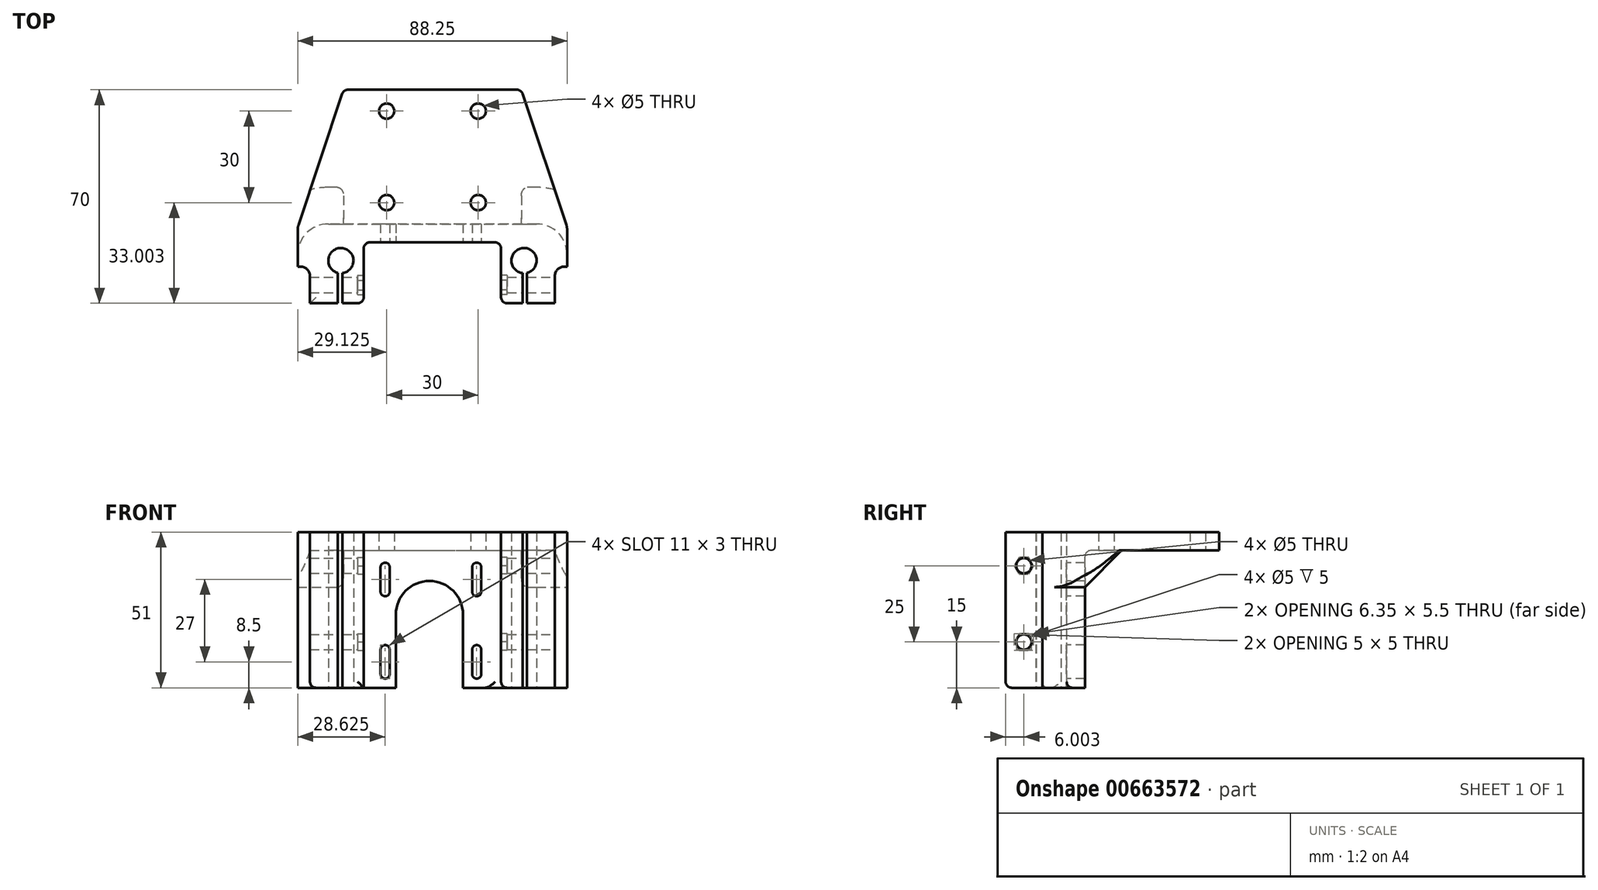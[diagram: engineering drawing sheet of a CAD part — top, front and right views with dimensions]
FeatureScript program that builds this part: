
annotation { "Feature Type Name" : "Feature", "Feature Type Description" : "" }
export const myFeature = defineFeature(function(context is Context, id is Id, definition is map)
    precondition{}
    {
        {
            var Q0;
            Q0=qCreatedBy(makeId("Top.planeOp"),FACE);
            var sketch = newSketch(context, id + "F0", { "sketchPlane" : qUnion([Q0])});
            skLineSegment(sketch, "E0.bottom", {"start": v(-36.85, 32.58) * mm, "end": v(21.4, 32.58) * mm});
            skLineSegment(sketch, "E0.top", {"start": v(-51.85, -37.42) * mm, "end": v(36.4, -37.42) * mm});
            skLineSegment(sketch, "E0.left", {"start": v(-51.85, -12.42) * mm, "end": v(-51.85, -37.42) * mm});
            skLineSegment(sketch, "E0.right", {"start": v(36.4, -12.42) * mm, "end": v(36.4, -37.42) * mm});
            skLineSegment(sketch, "E1", {"start": v(-30.23, -37.42) * mm, "end": v(-30.23, -17.42) * mm});
            skLineSegment(sketch, "E2", {"start": v(-30.23, -17.42) * mm, "end": v(14.77, -17.42) * mm});
            skLineSegment(sketch, "E3", {"start": v(14.77, -17.42) * mm, "end": v(14.77, -37.42) * mm});
            skCircle(sketch, "E4", {"center": v(22.27, -23.42) * mm, "radius": 4.12 * mm});
            skCircle(sketch, "E5", {"center": v(-37.73, -23.42) * mm, "radius": 4.12 * mm});
            skCircle(sketch, "E6", {"center": v(-22.73, 25.58) * mm, "radius": 2.5 * mm});
            skCircle(sketch, "E7", {"center": v(7.27, 25.58) * mm, "radius": 2.5 * mm});
            skCircle(sketch, "E8", {"center": v(-22.73, -4.42) * mm, "radius": 2.5 * mm});
            skCircle(sketch, "E9", {"center": v(7.27, -4.42) * mm, "radius": 2.5 * mm});
            skLineSegment(sketch, "E10", {"start": v(-51.85, -12.42) * mm, "end": v(-36.85, 32.58) * mm});
            skLineSegment(sketch, "E11", {"start": v(36.4, -12.42) * mm, "end": v(21.4, 32.58) * mm});
            skSolve(sketch);
        }
        {
            var Q0;
            Q0=makeQuery(id+"F0.imprint","IMPRINT",FACE,{"disambiguationData":[TD([[makeQuery(id+"F0.imprint","IMPRINT",EDGE,{"derivedFrom":sQuery(id+"F0.wireOp",EDGE,"E0.bottom")}),-1.0]])]});
            extrude(context, id + "F1", {"entities" : qUnion([Q0]), "depth" : 55 * mm, "offsetDistance" : 25 * mm});
        }
        {
            var Q0;
            Q0=makeQuery(id+"F1.opExtrude","CAP_FACE",FACE,{"disambiguationData":[OSD([sQuery(id+"F0.wireOp",EDGE,"E0.bottom"),sQuery(id+"F0.wireOp",EDGE,"E0.top"),sQuery(id+"F0.wireOp",EDGE,"E0.left"),sQuery(id+"F0.wireOp",EDGE,"E0.right"),sQuery(id+"F0.wireOp",EDGE,"E1"),sQuery(id+"F0.wireOp",EDGE,"E2"),sQuery(id+"F0.wireOp",EDGE,"E3"),sQuery(id+"F0.wireOp",EDGE,"E4"),sQuery(id+"F0.wireOp",EDGE,"E5"),sQuery(id+"F0.wireOp",EDGE,"E6"),sQuery(id+"F0.wireOp",EDGE,"E7"),sQuery(id+"F0.wireOp",EDGE,"E8"),sQuery(id+"F0.wireOp",EDGE,"E9"),sQuery(id+"F0.wireOp",EDGE,"E10"),sQuery(id+"F0.wireOp",EDGE,"E11")])],"isStart":true});
            var sketch = newSketch(context, id + "F2", { "sketchPlane" : qUnion([Q0])});
            skLineSegment(sketch, "E12", {"start": v(30.89, -4.12) * mm, "end": v(16.4, 11.42) * mm});
            skLineSegment(sketch, "E13", {"start": v(16.4, 11.42) * mm, "end": v(-31.85, 11.42) * mm});
            skLineSegment(sketch, "E14", {"start": v(-31.85, 11.42) * mm, "end": v(-46.34, -4.12) * mm});
            skLineSegment(sketch, "E15", {"start": v(-46.34, -4.12) * mm, "end": v(-36.85, -32.58) * mm});
            skLineSegment(sketch, "E16", {"start": v(-36.85, -32.58) * mm, "end": v(21.4, -32.58) * mm});
            skLineSegment(sketch, "E17", {"start": v(21.4, -32.58) * mm, "end": v(30.89, -4.12) * mm});
            skSolve(sketch);
        }
        {
            var Q0;
            Q0=makeQuery(id+"F2.imprint","IMPRINT",FACE,{"disambiguationData":[TD([[makeQuery(id+"F2.imprint","IMPRINT",EDGE,{"derivedFrom":sQuery(id+"F2.wireOp",EDGE,"E12")}),1.0]])]});
            extrude(context, id + "F3", {"entities" : qUnion([Q0]), "operationType" : NewBodyOperationType.REMOVE, "oppositeDirection" : true, "depth" : 45 * mm, "offsetDistance" : 25 * mm});
        }
        {
            var Q0;
            Q0=makeQuery(id+"F1.opExtrude","SWEPT_FACE",FACE,{"disambiguationData":[OSD([sQuery(id+"F0.wireOp",EDGE,"E2")])]});
            var sketch = newSketch(context, id + "F4", { "sketchPlane" : qUnion([Q0])});
            skArc(sketch, "E18", {"start": v(2.27, 24) * mm, "mid": v(-8.73, 35) * mm, "end": v(-19.73, 24) * mm});
            skLineSegment(sketch, "E19", {"start": v(-19.73, 24) * mm, "end": v(-19.73, 0) * mm});
            skLineSegment(sketch, "E20", {"start": v(-19.73, 0) * mm, "end": v(2.27, 0) * mm});
            skLineSegment(sketch, "E21", {"start": v(2.27, 24) * mm, "end": v(2.27, 0) * mm});
            skSolve(sketch);
        }
        {
            var Q0;
            Q0=makeQuery(id+"F4.imprint","IMPRINT",FACE,{"disambiguationData":[TD([[makeQuery(id+"F4.imprint","IMPRINT",EDGE,{"derivedFrom":sQuery(id+"F4.wireOp",EDGE,"E18")}),1.0]])]});
            extrude(context, id + "F5", {"entities" : qUnion([Q0]), "operationType" : NewBodyOperationType.REMOVE, "oppositeDirection" : true, "depth" : 25 * mm, "offsetDistance" : 25 * mm});
        }
        {
            var Q0;
            {var subQ0=sQuery(id+"F0.wireOp",EDGE,"E1");var subQ1=sQuery(id+"F0.wireOp",EDGE,"E0.left");var subQ2=sQuery(id+"F0.wireOp",EDGE,"E10");var subQ3=sQuery(id+"F0.wireOp",EDGE,"E2");var subQ4=sQuery(id+"F0.wireOp",EDGE,"E0.top");var subQ5=sQuery(id+"F0.wireOp",EDGE,"E5");Q0=makeQuery(id+"F5.boolean.opBoolean","SPLIT",FACE,{"disambiguationData":[TD([makeQuery(id+"F1.opExtrude","SWEPT_FACE",FACE,{"disambiguationData":[OSD([subQ1])]})])],"derivedFrom":makeQuery(id+"F1.opExtrude","CAP_FACE",FACE,{"disambiguationData":[OSD([sQuery(id+"F0.wireOp",EDGE,"E0.bottom"),subQ4,subQ1,sQuery(id+"F0.wireOp",EDGE,"E0.right"),subQ0,subQ3,sQuery(id+"F0.wireOp",EDGE,"E3"),sQuery(id+"F0.wireOp",EDGE,"E4"),subQ5,sQuery(id+"F0.wireOp",EDGE,"E6"),sQuery(id+"F0.wireOp",EDGE,"E7"),sQuery(id+"F0.wireOp",EDGE,"E8"),sQuery(id+"F0.wireOp",EDGE,"E9"),subQ2,sQuery(id+"F0.wireOp",EDGE,"E11")])],"isStart":true})});}
            var sketch = newSketch(context, id + "F6", { "sketchPlane" : qUnion([Q0])});
            skLineSegment(sketch, "E22.bottom", {"start": v(-38.73, 37.42) * mm, "end": v(-37.23, 37.42) * mm});
            skLineSegment(sketch, "E22.top", {"start": v(-38.73, 26.54) * mm, "end": v(-37.23, 26.54) * mm});
            skLineSegment(sketch, "E22.left", {"start": v(-38.73, 37.42) * mm, "end": v(-38.73, 26.54) * mm});
            skLineSegment(sketch, "E22.right", {"start": v(-37.23, 37.42) * mm, "end": v(-37.23, 26.54) * mm});
            skLineSegment(sketch, "E23.bottom", {"start": v(21.77, 37.42) * mm, "end": v(23.27, 37.42) * mm});
            skLineSegment(sketch, "E23.top", {"start": v(21.77, 26.54) * mm, "end": v(23.27, 26.54) * mm});
            skLineSegment(sketch, "E23.left", {"start": v(21.77, 37.42) * mm, "end": v(21.77, 26.54) * mm});
            skLineSegment(sketch, "E23.right", {"start": v(23.27, 37.42) * mm, "end": v(23.27, 26.54) * mm});
            skSolve(sketch);
        }
        {
            var Q0;
            Q0=makeQuery(id+"F6.imprint","IMPRINT",FACE,{"disambiguationData":[TD([[makeQuery(id+"F6.imprint","IMPRINT",EDGE,{"derivedFrom":sQuery(id+"F6.wireOp",EDGE,"E23.bottom")}),-1.0]])]});
            var Q1;
            {var subQ0=sQuery(id+"F6.wireOp",EDGE,"E22.bottom");Q1=makeQuery(id+"F6.imprint","IMPRINT",FACE,{"disambiguationData":[TD([[makeQuery(id+"F6.imprint","IMPRINT",EDGE,{"derivedFrom":subQ0}),-1.0]])]});}
            extrude(context, id + "F7", {"entities" : qUnion([Q0, Q1]), "operationType" : NewBodyOperationType.REMOVE, "oppositeDirection" : true, "depth" : 55 * mm, "offsetDistance" : 25 * mm});
        }
        {
            var Q0;
            Q0=makeQuery(id+"F1.opExtrude","SWEPT_FACE",FACE,{"disambiguationData":[OSD([sQuery(id+"F0.wireOp",EDGE,"E0.right")])]});
            var sketch = newSketch(context, id + "F8", { "sketchPlane" : qUnion([Q0])});
            skCircle(sketch, "E24", {"center": v(-31.42, 15) * mm, "radius": 2.5 * mm});
            skCircle(sketch, "E25", {"center": v(-31.42, 40) * mm, "radius": 2.5 * mm});
            skSolve(sketch);
        }
        {
            var Q0;
            Q0=makeQuery(id+"F8.imprint","IMPRINT",FACE,{"disambiguationData":[TD([[makeQuery(id+"F8.imprint","IMPRINT",EDGE,{"derivedFrom":sQuery(id+"F8.wireOp",EDGE,"E24")}),1.0]])]});
            var Q1;
            Q1=makeQuery(id+"F8.imprint","IMPRINT",FACE,{"disambiguationData":[TD([[makeQuery(id+"F8.imprint","IMPRINT",EDGE,{"derivedFrom":sQuery(id+"F8.wireOp",EDGE,"E25")}),1.0]])]});
            extrude(context, id + "F9", {"entities" : qUnion([Q0, Q1]), "operationType" : NewBodyOperationType.REMOVE, "oppositeDirection" : true, "depth" : 100 * mm, "offsetDistance" : 25 * mm});
        }
        {
            var Q0;
            Q0=makeQuery(id+"F1.opExtrude","SWEPT_FACE",FACE,{"disambiguationData":[OSD([sQuery(id+"F0.wireOp",EDGE,"E0.bottom")])]});
            var sketch = newSketch(context, id + "F10", { "sketchPlane" : qUnion([Q0])});
            skLineSegment(sketch, "E26", {"start": v(51.85, 51) * mm, "end": v(-36.4, 51) * mm});
            skLineSegment(sketch, "E27", {"start": v(51.85, 51) * mm, "end": v(51.85, 51) * mm});
            skLineSegment(sketch, "E28", {"start": v(-36.4, 51) * mm, "end": v(-36.4, 51) * mm});
            skLineSegment(sketch, "E29", {"start": v(-36.4, 51) * mm, "end": v(-36.4, 55) * mm});
            skLineSegment(sketch, "E30", {"start": v(-36.4, 55) * mm, "end": v(51.85, 55) * mm});
            skLineSegment(sketch, "E31", {"start": v(51.85, 55) * mm, "end": v(51.85, 51) * mm});
            skSolve(sketch);
        }
        {
            var Q0;
            {var subQ0=sQuery(id+"F10.wireOp",EDGE,"E31");Q0=makeQuery(id+"F10.imprint","IMPRINT",FACE,{"disambiguationData":[TD([[makeQuery(id+"F10.imprint","IMPRINT",EDGE,{"derivedFrom":subQ0}),-1.0]])]});}
            var Q1;
            {var subQ0=sQuery(id+"F10.wireOp",EDGE,"E26");var subQ1=sQuery(id+"F0.wireOp",EDGE,"E0.bottom");var subQ2=makeQuery(id+"F1.opExtrude","SWEPT_EDGE",EDGE,{"disambiguationData":[OSD([subQ1,sQuery(id+"F0.wireOp",EDGE,"E10")])]});var subQ3=makeQuery(id+"F10.imprint","INTERSECT",VERTEX,{"derivedFrom":[subQ2,subQ0]});Q1=makeQuery(id+"F10.imprint","IMPRINT",FACE,{"disambiguationData":[TD([[makeQuery(id+"F10.imprint","IMPRINT",EDGE,{"disambiguationData":[TD([[subQ3,-1.0]])],"derivedFrom":subQ0}),-1.0]])]});}
            var Q2;
            {var subQ0=sQuery(id+"F10.wireOp",EDGE,"E29");Q2=makeQuery(id+"F10.imprint","IMPRINT",FACE,{"disambiguationData":[TD([[makeQuery(id+"F10.imprint","IMPRINT",EDGE,{"derivedFrom":subQ0}),-1.0]])]});}
            extrude(context, id + "F11", {"entities" : qUnion([Q0, Q1, Q2]), "operationType" : NewBodyOperationType.REMOVE, "oppositeDirection" : true, "depth" : 80 * mm, "offsetDistance" : 25 * mm});
        }
        {
            var Q0;
            Q0=makeQuery(id+"F1.opExtrude","SWEPT_FACE",FACE,{"disambiguationData":[OSD([sQuery(id+"F0.wireOp",EDGE,"E2")])]});
            var sketch = newSketch(context, id + "F12", { "sketchPlane" : qUnion([Q0])});
            skArc(sketch, "E32", {"start": v(-21.73, 39.5) * mm, "mid": v(-23.23, 41) * mm, "end": v(-24.73, 39.5) * mm});
            skArc(sketch, "E33", {"start": v(8.27, 39.5) * mm, "mid": v(6.77, 41) * mm, "end": v(5.27, 39.5) * mm});
            skArc(sketch, "E34", {"start": v(5.27, 4.5) * mm, "mid": v(6.77, 3) * mm, "end": v(8.27, 4.5) * mm});
            skArc(sketch, "E35", {"start": v(-24.73, 4.5) * mm, "mid": v(-23.23, 3) * mm, "end": v(-21.73, 4.5) * mm});
            skLineSegment(sketch, "E36", {"start": v(-21.73, 4.5) * mm, "end": v(-21.73, 12.5) * mm});
            skLineSegment(sketch, "E37", {"start": v(8.27, 39.5) * mm, "end": v(8.27, 31.5) * mm});
            skLineSegment(sketch, "E38", {"start": v(5.27, 4.5) * mm, "end": v(5.27, 12.5) * mm});
            skLineSegment(sketch, "E39", {"start": v(-24.73, 39.5) * mm, "end": v(-24.73, 31.5) * mm});
            skArc(sketch, "E40", {"start": v(8.27, 12.5) * mm, "mid": v(6.77, 14) * mm, "end": v(5.27, 12.5) * mm});
            skArc(sketch, "E41", {"start": v(5.27, 31.5) * mm, "mid": v(6.77, 30) * mm, "end": v(8.27, 31.5) * mm});
            skArc(sketch, "E42", {"start": v(-24.73, 31.5) * mm, "mid": v(-23.23, 30) * mm, "end": v(-21.73, 31.5) * mm});
            skArc(sketch, "E43", {"start": v(-21.73, 12.5) * mm, "mid": v(-23.23, 14) * mm, "end": v(-24.73, 12.5) * mm});
            skLineSegment(sketch, "E44.trimOffspring", {"start": v(8.27, 12.5) * mm, "end": v(8.27, 4.5) * mm});
            skLineSegment(sketch, "E45.trimOffspring", {"start": v(5.27, 31.5) * mm, "end": v(5.27, 39.5) * mm});
            skLineSegment(sketch, "E46.trimOffspring", {"start": v(-21.73, 31.5) * mm, "end": v(-21.73, 39.5) * mm});
            skLineSegment(sketch, "E47.trimOffspring", {"start": v(-24.73, 12.5) * mm, "end": v(-24.73, 4.5) * mm});
            skSolve(sketch);
        }
        {
            var Q0;
            Q0=makeQuery(id+"F12.imprint","IMPRINT",FACE,{"disambiguationData":[TD([[makeQuery(id+"F12.imprint","IMPRINT",EDGE,{"derivedFrom":sQuery(id+"F12.wireOp",EDGE,"E32")}),1.0]])]});
            var Q1;
            Q1=makeQuery(id+"F12.imprint","IMPRINT",FACE,{"disambiguationData":[TD([[makeQuery(id+"F12.imprint","IMPRINT",EDGE,{"derivedFrom":sQuery(id+"F12.wireOp",EDGE,"E35")}),1.0]])]});
            var Q2;
            Q2=makeQuery(id+"F12.imprint","IMPRINT",FACE,{"disambiguationData":[TD([[makeQuery(id+"F12.imprint","IMPRINT",EDGE,{"derivedFrom":sQuery(id+"F12.wireOp",EDGE,"E34")}),1.0]])]});
            var Q3;
            Q3=makeQuery(id+"F12.imprint","IMPRINT",FACE,{"disambiguationData":[TD([[makeQuery(id+"F12.imprint","IMPRINT",EDGE,{"derivedFrom":sQuery(id+"F12.wireOp",EDGE,"E33")}),1.0]])]});
            extrude(context, id + "F13", {"entities" : qUnion([Q0, Q1, Q2, Q3]), "operationType" : NewBodyOperationType.REMOVE, "oppositeDirection" : true, "depth" : 25 * mm, "offsetDistance" : 25 * mm});
        }
        {
            var Q0;
            {var subQ0=sQuery(id+"F0.wireOp",EDGE,"E1");var subQ1=sQuery(id+"F0.wireOp",EDGE,"E0.left");var subQ2=sQuery(id+"F0.wireOp",EDGE,"E10");var subQ3=sQuery(id+"F0.wireOp",EDGE,"E2");var subQ4=sQuery(id+"F0.wireOp",EDGE,"E0.top");var subQ5=sQuery(id+"F0.wireOp",EDGE,"E5");Q0=makeQuery(id+"F5.boolean.opBoolean","SPLIT",FACE,{"disambiguationData":[TD([makeQuery(id+"F1.opExtrude","SWEPT_FACE",FACE,{"disambiguationData":[OSD([subQ1])]})])],"derivedFrom":makeQuery(id+"F1.opExtrude","CAP_FACE",FACE,{"disambiguationData":[OSD([sQuery(id+"F0.wireOp",EDGE,"E0.bottom"),subQ4,subQ1,sQuery(id+"F0.wireOp",EDGE,"E0.right"),subQ0,subQ3,sQuery(id+"F0.wireOp",EDGE,"E3"),sQuery(id+"F0.wireOp",EDGE,"E4"),subQ5,sQuery(id+"F0.wireOp",EDGE,"E6"),sQuery(id+"F0.wireOp",EDGE,"E7"),sQuery(id+"F0.wireOp",EDGE,"E8"),sQuery(id+"F0.wireOp",EDGE,"E9"),subQ2,sQuery(id+"F0.wireOp",EDGE,"E11")])],"isStart":true})});}
            var sketch = newSketch(context, id + "F14", { "sketchPlane" : qUnion([Q0])});
            skLineSegment(sketch, "E48", {"start": v(-46.34, -4.12) * mm, "end": v(-31.85, 11.42) * mm});
            skLineSegment(sketch, "E49", {"start": v(-31.85, 11.42) * mm, "end": v(-51.52, 11.42) * mm});
            skLineSegment(sketch, "E50", {"start": v(-51.52, 11.42) * mm, "end": v(-46.34, -4.12) * mm});
            skLineSegment(sketch, "E51", {"start": v(16.4, 11.42) * mm, "end": v(30.89, -4.12) * mm});
            skLineSegment(sketch, "E52", {"start": v(30.89, -4.12) * mm, "end": v(36.07, 11.42) * mm});
            skLineSegment(sketch, "E53", {"start": v(36.07, 11.42) * mm, "end": v(16.4, 11.42) * mm});
            skSolve(sketch);
        }
        {
            var Q0;
            Q0=makeQuery(id+"F14.imprint","IMPRINT",FACE,{"disambiguationData":[TD([[makeQuery(id+"F14.imprint","IMPRINT",EDGE,{"derivedFrom":sQuery(id+"F14.wireOp",EDGE,"E48")}),-1.0]])]});
            var Q1;
            Q1=makeQuery(id+"F14.imprint","IMPRINT",FACE,{"disambiguationData":[TD([[makeQuery(id+"F14.imprint","IMPRINT",EDGE,{"derivedFrom":sQuery(id+"F14.wireOp",EDGE,"E51")}),1.0]])]});
            extrude(context, id + "F15", {"entities" : qUnion([Q0, Q1]), "operationType" : NewBodyOperationType.REMOVE, "oppositeDirection" : true, "depth" : 45 * mm, "offsetDistance" : 25 * mm});
        }
        {
            var Q0;
            {var subQ0=sQuery(id+"F0.wireOp",EDGE,"E1");var subQ1=sQuery(id+"F0.wireOp",EDGE,"E0.left");var subQ2=sQuery(id+"F0.wireOp",EDGE,"E10");var subQ3=sQuery(id+"F0.wireOp",EDGE,"E2");var subQ4=sQuery(id+"F0.wireOp",EDGE,"E0.top");var subQ5=sQuery(id+"F0.wireOp",EDGE,"E5");Q0=makeQuery(id+"F5.boolean.opBoolean","SPLIT",FACE,{"disambiguationData":[TD([makeQuery(id+"F1.opExtrude","SWEPT_FACE",FACE,{"disambiguationData":[OSD([subQ1])]})])],"derivedFrom":makeQuery(id+"F1.opExtrude","CAP_FACE",FACE,{"disambiguationData":[OSD([sQuery(id+"F0.wireOp",EDGE,"E0.bottom"),subQ4,subQ1,sQuery(id+"F0.wireOp",EDGE,"E0.right"),subQ0,subQ3,sQuery(id+"F0.wireOp",EDGE,"E3"),sQuery(id+"F0.wireOp",EDGE,"E4"),subQ5,sQuery(id+"F0.wireOp",EDGE,"E6"),sQuery(id+"F0.wireOp",EDGE,"E7"),sQuery(id+"F0.wireOp",EDGE,"E8"),sQuery(id+"F0.wireOp",EDGE,"E9"),subQ2,sQuery(id+"F0.wireOp",EDGE,"E11")])],"isStart":true})});}
            var sketch = newSketch(context, id + "F16", { "sketchPlane" : qUnion([Q0])});
            skArc(sketch, "E54", {"start": v(-51.85, 21.42) * mm, "mid": v(-48.92, 14.35) * mm, "end": v(-41.85, 11.42) * mm});
            skArc(sketch, "E55", {"start": v(26.4, 11.42) * mm, "mid": v(33.47, 14.35) * mm, "end": v(36.4, 21.42) * mm});
            skLineSegment(sketch, "E56", {"start": v(26.4, 11.42) * mm, "end": v(36.42, 11.42) * mm});
            skLineSegment(sketch, "E57", {"start": v(-51.85, 21.42) * mm, "end": v(-51.85, 11.42) * mm});
            skLineSegment(sketch, "E58", {"start": v(-51.85, 11.42) * mm, "end": v(-41.85, 11.42) * mm});
            skSolve(sketch);
        }
        {
            var Q0;
            {var subQ0=sQuery(id+"F16.wireOp",EDGE,"E54");Q0=makeQuery(id+"F16.imprint","IMPRINT",FACE,{"disambiguationData":[TD([[makeQuery(id+"F16.imprint","IMPRINT",EDGE,{"derivedFrom":subQ0}),-1.0]])]});}
            extrude(context, id + "F17", {"entities" : qUnion([Q0]), "operationType" : NewBodyOperationType.REMOVE, "oppositeDirection" : true, "depth" : 45 * mm, "offsetDistance" : 25 * mm});
        }
        {
            var Q0;
            {var subQ0=sQuery(id+"F0.wireOp",EDGE,"E2");var subQ1=sQuery(id+"F0.wireOp",EDGE,"E0.right");var subQ2=sQuery(id+"F0.wireOp",EDGE,"E11");var subQ3=sQuery(id+"F0.wireOp",EDGE,"E3");var subQ4=sQuery(id+"F0.wireOp",EDGE,"E0.top");var subQ5=sQuery(id+"F0.wireOp",EDGE,"E4");Q0=makeQuery(id+"F5.boolean.opBoolean","SPLIT",FACE,{"disambiguationData":[TD([makeQuery(id+"F1.opExtrude","SWEPT_FACE",FACE,{"disambiguationData":[OSD([subQ1])]})])],"derivedFrom":makeQuery(id+"F1.opExtrude","CAP_FACE",FACE,{"disambiguationData":[OSD([sQuery(id+"F0.wireOp",EDGE,"E0.bottom"),subQ4,sQuery(id+"F0.wireOp",EDGE,"E0.left"),subQ1,sQuery(id+"F0.wireOp",EDGE,"E1"),subQ0,subQ3,subQ5,sQuery(id+"F0.wireOp",EDGE,"E5"),sQuery(id+"F0.wireOp",EDGE,"E6"),sQuery(id+"F0.wireOp",EDGE,"E7"),sQuery(id+"F0.wireOp",EDGE,"E8"),sQuery(id+"F0.wireOp",EDGE,"E9"),sQuery(id+"F0.wireOp",EDGE,"E10"),subQ2])],"isStart":true})});}
            var sketch = newSketch(context, id + "F18", { "sketchPlane" : qUnion([Q0])});
            skArc(sketch, "E59", {"start": v(26.4, 11.42) * mm, "mid": v(33.47, 14.35) * mm, "end": v(36.4, 21.42) * mm});
            skSolve(sketch);
        }
        {
            var Q0;
            {var subQ0=sQuery(id+"F18.wireOp",EDGE,"E59");Q0=makeQuery(id+"F18.imprint","IMPRINT",FACE,{"disambiguationData":[TD([[makeQuery(id+"F18.imprint","IMPRINT",EDGE,{"derivedFrom":subQ0}),-1.0]])]});}
            extrude(context, id + "F19", {"entities" : qUnion([Q0]), "operationType" : NewBodyOperationType.REMOVE, "oppositeDirection" : true, "depth" : 45 * mm, "offsetDistance" : 25 * mm});
        }
        {
            var Q0;
            Q0=makeQuery(id+"F1.opExtrude","SWEPT_FACE",FACE,{"disambiguationData":[OSD([sQuery(id+"F0.wireOp",EDGE,"E1")])]});
            var sketch = newSketch(context, id + "F20", { "sketchPlane" : qUnion([Q0])});
            skCircle(sketch, "E60.cCircle", {"center": v(-31.42, 15) * mm, "radius": 2.75 * mm, "construction": true});
            skLineSegment(sketch, "E60.0", {"start": v(-29.83, 12.25) * mm, "end": v(-33, 12.25) * mm});
            skLineSegment(sketch, "E60.1", {"start": v(-33, 12.25) * mm, "end": v(-34.6, 15) * mm});
            skLineSegment(sketch, "E60.2", {"start": v(-34.6, 15) * mm, "end": v(-33, 17.75) * mm});
            skLineSegment(sketch, "E60.3", {"start": v(-33, 17.75) * mm, "end": v(-29.83, 17.75) * mm});
            skLineSegment(sketch, "E60.4", {"start": v(-29.83, 17.75) * mm, "end": v(-28.24, 15) * mm});
            skLineSegment(sketch, "E60.5", {"start": v(-28.24, 15) * mm, "end": v(-29.83, 12.25) * mm});
            skPoint(sketch, "E60.0.midPoint", {"position": v(-31.42, 12.25) * mm});
            skCircle(sketch, "E61.cCircle", {"center": v(-31.42, 40) * mm, "radius": 2.75 * mm, "construction": true});
            skLineSegment(sketch, "E61.0", {"start": v(-29.83, 37.25) * mm, "end": v(-33, 37.25) * mm});
            skLineSegment(sketch, "E61.1", {"start": v(-33, 37.25) * mm, "end": v(-34.6, 40) * mm});
            skLineSegment(sketch, "E61.2", {"start": v(-34.6, 40) * mm, "end": v(-33, 42.75) * mm});
            skLineSegment(sketch, "E61.3", {"start": v(-33, 42.75) * mm, "end": v(-29.83, 42.75) * mm});
            skLineSegment(sketch, "E61.4", {"start": v(-29.83, 42.75) * mm, "end": v(-28.24, 40) * mm});
            skLineSegment(sketch, "E61.5", {"start": v(-28.24, 40) * mm, "end": v(-29.83, 37.25) * mm});
            skPoint(sketch, "E61.0.midPoint", {"position": v(-31.42, 37.25) * mm});
            skSolve(sketch);
        }
        {
            var Q0;
            Q0=makeQuery(id+"F20.imprint","IMPRINT",FACE,{"disambiguationData":[TD([[makeQuery(id+"F20.imprint","IMPRINT",EDGE,{"derivedFrom":sQuery(id+"F20.wireOp",EDGE,"E60.0")}),-1.0]])]});
            var Q1;
            Q1=makeQuery(id+"F20.imprint","IMPRINT",FACE,{"disambiguationData":[TD([[makeQuery(id+"F20.imprint","IMPRINT",EDGE,{"derivedFrom":sQuery(id+"F20.wireOp",EDGE,"E61.0")}),-1.0]])]});
            extrude(context, id + "F21", {"entities" : qUnion([Q0, Q1]), "operationType" : NewBodyOperationType.REMOVE, "oppositeDirection" : true, "depth" : 2 * mm, "offsetDistance" : 25 * mm});
        }
        {
            var Q0;
            Q0=makeQuery(id+"F1.opExtrude","SWEPT_FACE",FACE,{"disambiguationData":[OSD([sQuery(id+"F0.wireOp",EDGE,"E3")])]});
            var sketch = newSketch(context, id + "F22", { "sketchPlane" : qUnion([Q0])});
            skCircle(sketch, "E62.cCircle", {"center": v(31.42, 15) * mm, "radius": 2.75 * mm, "construction": true});
            skLineSegment(sketch, "E62.0", {"start": v(33, 12.25) * mm, "end": v(29.83, 12.25) * mm});
            skLineSegment(sketch, "E62.1", {"start": v(29.83, 12.25) * mm, "end": v(28.24, 15) * mm});
            skLineSegment(sketch, "E62.2", {"start": v(28.24, 15) * mm, "end": v(29.83, 17.75) * mm});
            skLineSegment(sketch, "E62.3", {"start": v(29.83, 17.75) * mm, "end": v(33, 17.75) * mm});
            skLineSegment(sketch, "E62.4", {"start": v(33, 17.75) * mm, "end": v(34.6, 15) * mm});
            skLineSegment(sketch, "E62.5", {"start": v(34.6, 15) * mm, "end": v(33, 12.25) * mm});
            skPoint(sketch, "E62.0.midPoint", {"position": v(31.42, 12.25) * mm});
            skCircle(sketch, "E63.cCircle", {"center": v(31.42, 40) * mm, "radius": 2.75 * mm, "construction": true});
            skLineSegment(sketch, "E63.0", {"start": v(33, 37.25) * mm, "end": v(29.83, 37.25) * mm});
            skLineSegment(sketch, "E63.1", {"start": v(29.83, 37.25) * mm, "end": v(28.24, 40) * mm});
            skLineSegment(sketch, "E63.2", {"start": v(28.24, 40) * mm, "end": v(29.83, 42.75) * mm});
            skLineSegment(sketch, "E63.3", {"start": v(29.83, 42.75) * mm, "end": v(33, 42.75) * mm});
            skLineSegment(sketch, "E63.4", {"start": v(33, 42.75) * mm, "end": v(34.6, 40) * mm});
            skLineSegment(sketch, "E63.5", {"start": v(34.6, 40) * mm, "end": v(33, 37.25) * mm});
            skPoint(sketch, "E63.0.midPoint", {"position": v(31.42, 37.25) * mm});
            skSolve(sketch);
        }
        {
            var Q0;
            Q0=makeQuery(id+"F22.imprint","IMPRINT",FACE,{"disambiguationData":[TD([[makeQuery(id+"F22.imprint","IMPRINT",EDGE,{"derivedFrom":sQuery(id+"F22.wireOp",EDGE,"E62.0")}),-1.0]])]});
            var Q1;
            Q1=makeQuery(id+"F22.imprint","IMPRINT",FACE,{"disambiguationData":[TD([[makeQuery(id+"F22.imprint","IMPRINT",EDGE,{"derivedFrom":sQuery(id+"F22.wireOp",EDGE,"E63.0")}),-1.0]])]});
            extrude(context, id + "F23", {"entities" : qUnion([Q0, Q1]), "operationType" : NewBodyOperationType.REMOVE, "oppositeDirection" : true, "depth" : 2 * mm, "offsetDistance" : 25 * mm});
        }
        {
            var Q0;
            Q0=makeQuery(id+"F11.boolean.opBoolean","COPY",FACE,{"derivedFrom":makeQuery(id+"F11.opExtrude","SWEPT_FACE",FACE,{"disambiguationData":[OSD([sQuery(id+"F10.wireOp",EDGE,"E26")])]})});
            var sketch = newSketch(context, id + "F24", { "sketchPlane" : qUnion([Q0])});
            skLineSegment(sketch, "E64.bottom", {"start": v(36.4, -37.42) * mm, "end": v(32.4, -37.42) * mm});
            skLineSegment(sketch, "E64.top", {"start": v(36.4, -25.42) * mm, "end": v(35.4, -25.42) * mm});
            skLineSegment(sketch, "E64.left", {"start": v(36.4, -37.42) * mm, "end": v(36.4, -25.42) * mm});
            skLineSegment(sketch, "E64.right", {"start": v(32.4, -37.42) * mm, "end": v(32.4, -28.42) * mm});
            skPoint(sketch, "E65.visualSharp", {"position": v(32.4, -25.42) * mm});
            skArc(sketch, "E65.filletArc", {"start": v(35.4, -25.42) * mm, "mid": v(33.28, -26.3) * mm, "end": v(32.4, -28.42) * mm});
            skLineSegment(sketch, "E66.bottom", {"start": v(-51.85, -37.42) * mm, "end": v(-47.85, -37.42) * mm});
            skLineSegment(sketch, "E66.top", {"start": v(-51.85, -25.42) * mm, "end": v(-50.85, -25.42) * mm});
            skLineSegment(sketch, "E66.left", {"start": v(-51.85, -37.42) * mm, "end": v(-51.85, -25.42) * mm});
            skLineSegment(sketch, "E66.right", {"start": v(-47.85, -37.42) * mm, "end": v(-47.85, -28.42) * mm});
            skPoint(sketch, "E67.visualSharp", {"position": v(-47.85, -25.42) * mm});
            skArc(sketch, "E67.filletArc", {"start": v(-47.85, -28.42) * mm, "mid": v(-48.73, -26.3) * mm, "end": v(-50.85, -25.42) * mm});
            skSolve(sketch);
        }
        {
            var Q0;
            Q0=makeQuery(id+"F24.imprint","IMPRINT",FACE,{"disambiguationData":[TD([[makeQuery(id+"F24.imprint","IMPRINT",EDGE,{"derivedFrom":sQuery(id+"F24.wireOp",EDGE,"E64.bottom")}),1.0]])]});
            var Q1;
            Q1=makeQuery(id+"F24.imprint","IMPRINT",FACE,{"disambiguationData":[TD([[makeQuery(id+"F24.imprint","IMPRINT",EDGE,{"derivedFrom":sQuery(id+"F24.wireOp",EDGE,"E66.bottom")}),1.0]])]});
            extrude(context, id + "F25", {"entities" : qUnion([Q0, Q1]), "operationType" : NewBodyOperationType.REMOVE, "oppositeDirection" : true, "depth" : 60 * mm, "offsetDistance" : 25 * mm});
        }
        {
            var Q0;
            Q0=makeQuery(id+"F25.boolean.opBoolean","COPY",EDGE,{"derivedFrom":makeQuery(id+"F25.opExtrude","SWEPT_EDGE",EDGE,{"disambiguationData":[OSD([sQuery(id+"F10.wireOp",EDGE,"E26"),sQuery(id+"F10.wireOp",EDGE,"E29"),sQuery(id+"F24.wireOp",EDGE,"E64.top"),sQuery(id+"F24.wireOp",EDGE,"E64.left")])]})});
            var Q1;
            Q1=makeQuery(id+"F25.boolean.opBoolean","COPY",EDGE,{"derivedFrom":makeQuery(id+"F25.opExtrude","SWEPT_EDGE",EDGE,{"disambiguationData":[OSD([sQuery(id+"F10.wireOp",EDGE,"E26"),sQuery(id+"F10.wireOp",EDGE,"E31"),sQuery(id+"F24.wireOp",EDGE,"E66.top"),sQuery(id+"F24.wireOp",EDGE,"E66.left")])]})});
            var Q2;
            Q2=makeQuery(id+"F1.opExtrude","SWEPT_EDGE",EDGE,{"disambiguationData":[OSD([sQuery(id+"F0.wireOp",EDGE,"E0.left"),sQuery(id+"F0.wireOp",EDGE,"E10")])]});
            var Q3;
            Q3=makeQuery(id+"F1.opExtrude","SWEPT_EDGE",EDGE,{"disambiguationData":[OSD([sQuery(id+"F0.wireOp",EDGE,"E0.right"),sQuery(id+"F0.wireOp",EDGE,"E11")])]});
            fillet(context, id + "F26", {"entities" : qUnion([Q0, Q1, Q2, Q3]), "radius" : 5 * mm, "tangentPropagation" : true, "allowEdgeOverflow" : false});
        }
        {
            var Q0;
            Q0=makeQuery(id+"F1.opExtrude","SWEPT_EDGE",EDGE,{"disambiguationData":[OSD([sQuery(id+"F0.wireOp",EDGE,"E0.top"),sQuery(id+"F0.wireOp",EDGE,"E1")])]});
            var Q1;
            Q1=makeQuery(id+"F25.boolean.opBoolean","COPY",EDGE,{"derivedFrom":makeQuery(id+"F25.opExtrude","SWEPT_EDGE",EDGE,{"disambiguationData":[OSD([sQuery(id+"F0.wireOp",EDGE,"E0.top"),sQuery(id+"F10.wireOp",EDGE,"E26"),sQuery(id+"F24.wireOp",EDGE,"E66.bottom"),sQuery(id+"F24.wireOp",EDGE,"E66.right")])]})});
            var Q2;
            Q2=makeQuery(id+"F1.opExtrude","SWEPT_EDGE",EDGE,{"disambiguationData":[OSD([sQuery(id+"F0.wireOp",EDGE,"E0.top"),sQuery(id+"F0.wireOp",EDGE,"E3")])]});
            var Q3;
            Q3=makeQuery(id+"F25.boolean.opBoolean","COPY",EDGE,{"derivedFrom":makeQuery(id+"F25.opExtrude","SWEPT_EDGE",EDGE,{"disambiguationData":[OSD([sQuery(id+"F0.wireOp",EDGE,"E0.top"),sQuery(id+"F10.wireOp",EDGE,"E26"),sQuery(id+"F24.wireOp",EDGE,"E64.bottom"),sQuery(id+"F24.wireOp",EDGE,"E64.right")])]})});
            var Q4;
            Q4=makeQuery(id+"F1.opExtrude","SWEPT_EDGE",EDGE,{"disambiguationData":[OSD([sQuery(id+"F0.wireOp",EDGE,"E2"),sQuery(id+"F0.wireOp",EDGE,"E3")])]});
            var Q5;
            Q5=makeQuery(id+"F1.opExtrude","SWEPT_EDGE",EDGE,{"disambiguationData":[OSD([sQuery(id+"F0.wireOp",EDGE,"E1"),sQuery(id+"F0.wireOp",EDGE,"E2")])]});
            var Q6;
            Q6=makeQuery(id+"F17.boolean.opBoolean","MERGE",EDGE,{"derivedFrom":[makeQuery(id+"F15.boolean.opBoolean","MERGE",EDGE,{"derivedFrom":[makeQuery(id+"F3.boolean.opBoolean","COPY",EDGE,{"derivedFrom":makeQuery(id+"F3.opExtrude","CAP_EDGE",EDGE,{"disambiguationData":[OSD([sQuery(id+"F2.wireOp",EDGE,"E15")])],"isStart":false})}),makeQuery(id+"F15.opExtrude","CAP_EDGE",EDGE,{"disambiguationData":[OSD([sQuery(id+"F14.wireOp",EDGE,"E50")])],"isStart":false})]}),makeQuery(id+"F17.opExtrude","CAP_EDGE",EDGE,{"disambiguationData":[OSD([sQuery(id+"F0.wireOp",EDGE,"E10")])],"isStart":false})]});
            var Q7;
            Q7=makeQuery(id+"F3.boolean.opBoolean","COPY",EDGE,{"derivedFrom":makeQuery(id+"F3.opExtrude","CAP_EDGE",EDGE,{"disambiguationData":[OSD([sQuery(id+"F2.wireOp",EDGE,"E16")])],"isStart":false})});
            var Q8;
            Q8=makeQuery(id+"F19.boolean.opBoolean","MERGE",EDGE,{"derivedFrom":[makeQuery(id+"F15.boolean.opBoolean","MERGE",EDGE,{"derivedFrom":[makeQuery(id+"F3.boolean.opBoolean","COPY",EDGE,{"derivedFrom":makeQuery(id+"F3.opExtrude","CAP_EDGE",EDGE,{"disambiguationData":[OSD([sQuery(id+"F2.wireOp",EDGE,"E17")])],"isStart":false})}),makeQuery(id+"F15.opExtrude","CAP_EDGE",EDGE,{"disambiguationData":[OSD([sQuery(id+"F14.wireOp",EDGE,"E52")])],"isStart":false})]}),makeQuery(id+"F19.opExtrude","CAP_EDGE",EDGE,{"disambiguationData":[OSD([sQuery(id+"F0.wireOp",EDGE,"E11")])],"isStart":false})]});
            var Q9;
            Q9=makeQuery(id+"F1.opExtrude","SWEPT_EDGE",EDGE,{"disambiguationData":[OSD([sQuery(id+"F0.wireOp",EDGE,"E0.bottom"),sQuery(id+"F0.wireOp",EDGE,"E11")])]});
            var Q10;
            Q10=makeQuery(id+"F1.opExtrude","SWEPT_EDGE",EDGE,{"disambiguationData":[OSD([sQuery(id+"F0.wireOp",EDGE,"E0.bottom"),sQuery(id+"F0.wireOp",EDGE,"E10")])]});
            var Q11;
            {var subQ0=sQuery(id+"F0.wireOp",EDGE,"E1");var subQ1=sQuery(id+"F0.wireOp",EDGE,"E0.left");var subQ2=sQuery(id+"F0.wireOp",EDGE,"E10");var subQ3=sQuery(id+"F0.wireOp",EDGE,"E2");var subQ4=sQuery(id+"F0.wireOp",EDGE,"E0.top");var subQ5=sQuery(id+"F0.wireOp",EDGE,"E5");Q11=makeQuery(id+"F25.boolean.opBoolean","INTERSECT",EDGE,{"derivedFrom":[makeQuery(id+"F5.boolean.opBoolean","SPLIT",FACE,{"disambiguationData":[TD([makeQuery(id+"F1.opExtrude","SWEPT_FACE",FACE,{"disambiguationData":[OSD([subQ1])]})])],"derivedFrom":makeQuery(id+"F1.opExtrude","CAP_FACE",FACE,{"disambiguationData":[OSD([sQuery(id+"F0.wireOp",EDGE,"E0.bottom"),subQ4,subQ1,sQuery(id+"F0.wireOp",EDGE,"E0.right"),subQ0,subQ3,sQuery(id+"F0.wireOp",EDGE,"E3"),sQuery(id+"F0.wireOp",EDGE,"E4"),subQ5,sQuery(id+"F0.wireOp",EDGE,"E6"),sQuery(id+"F0.wireOp",EDGE,"E7"),sQuery(id+"F0.wireOp",EDGE,"E8"),sQuery(id+"F0.wireOp",EDGE,"E9"),subQ2,sQuery(id+"F0.wireOp",EDGE,"E11")])],"isStart":true})}),makeQuery(id+"F25.opExtrude","SWEPT_FACE",FACE,{"disambiguationData":[OSD([sQuery(id+"F24.wireOp",EDGE,"E66.right")])]})]});}
            var Q12;
            {var subQ0=sQuery(id+"F0.wireOp",EDGE,"E2");var subQ1=sQuery(id+"F0.wireOp",EDGE,"E1");Q12=makeQuery(id+"F5.boolean.opBoolean","SPLIT",EDGE,{"disambiguationData":[TD([makeQuery(id+"F1.opExtrude","SWEPT_FACE",FACE,{"disambiguationData":[OSD([subQ1])]})])],"derivedFrom":makeQuery(id+"F1.opExtrude","CAP_EDGE",EDGE,{"disambiguationData":[OSD([subQ0])],"isStart":true})});}
            var Q13;
            {var subQ0=sQuery(id+"F0.wireOp",EDGE,"E1");var subQ1=sQuery(id+"F0.wireOp",EDGE,"E0.left");var subQ2=sQuery(id+"F0.wireOp",EDGE,"E0.top");var subQ3=makeQuery(id+"F0.imprint","IMPRINT",EDGE,{"disambiguationData":[TD([[makeQuery(id+"F0.imprint","INTERSECT",VERTEX,{"derivedFrom":[subQ2,subQ1]}),-1.0]])],"derivedFrom":subQ2});Q13=makeQuery(id+"F7.boolean.opBoolean","SPLIT",EDGE,{"disambiguationData":[TD([makeQuery(id+"F1.opExtrude","SWEPT_FACE",FACE,{"disambiguationData":[OSD([subQ0])]})])],"derivedFrom":makeQuery(id+"F1.opExtrude","CAP_EDGE",EDGE,{"disambiguationData":[OSD([subQ2]),TDD([subQ3])],"isStart":true})});}
            var Q14;
            {var subQ1=sQuery(id+"F0.wireOp",EDGE,"E0.left");var subQ2=sQuery(id+"F0.wireOp",EDGE,"E0.top");var subQ3=makeQuery(id+"F0.imprint","IMPRINT",EDGE,{"disambiguationData":[TD([[makeQuery(id+"F0.imprint","INTERSECT",VERTEX,{"derivedFrom":[subQ2,subQ1]}),-1.0]])],"derivedFrom":subQ2});Q14=makeQuery(id+"F7.boolean.opBoolean","SPLIT",EDGE,{"disambiguationData":[TD([makeQuery(id+"F1.opExtrude","SWEPT_FACE",FACE,{"disambiguationData":[OSD([subQ1])]})])],"derivedFrom":makeQuery(id+"F1.opExtrude","CAP_EDGE",EDGE,{"disambiguationData":[OSD([subQ2]),TDD([subQ3])],"isStart":true})});}
            var Q15;
            {var subQ1=sQuery(id+"F0.wireOp",EDGE,"E0.right");var subQ2=sQuery(id+"F0.wireOp",EDGE,"E0.top");var subQ3=makeQuery(id+"F0.imprint","IMPRINT",EDGE,{"disambiguationData":[TD([[makeQuery(id+"F0.imprint","INTERSECT",VERTEX,{"derivedFrom":[subQ2,subQ1]}),1.0]])],"derivedFrom":subQ2});Q15=makeQuery(id+"F7.boolean.opBoolean","SPLIT",EDGE,{"disambiguationData":[TD([makeQuery(id+"F1.opExtrude","SWEPT_FACE",FACE,{"disambiguationData":[OSD([subQ1])]})])],"derivedFrom":makeQuery(id+"F1.opExtrude","CAP_EDGE",EDGE,{"disambiguationData":[OSD([subQ2]),TDD([subQ3])],"isStart":true})});}
            var Q16;
            {var subQ0=sQuery(id+"F0.wireOp",EDGE,"E3");var subQ1=sQuery(id+"F0.wireOp",EDGE,"E0.right");var subQ2=sQuery(id+"F0.wireOp",EDGE,"E0.top");var subQ3=makeQuery(id+"F0.imprint","IMPRINT",EDGE,{"disambiguationData":[TD([[makeQuery(id+"F0.imprint","INTERSECT",VERTEX,{"derivedFrom":[subQ2,subQ1]}),1.0]])],"derivedFrom":subQ2});Q16=makeQuery(id+"F7.boolean.opBoolean","SPLIT",EDGE,{"disambiguationData":[TD([makeQuery(id+"F1.opExtrude","SWEPT_FACE",FACE,{"disambiguationData":[OSD([subQ0])]})])],"derivedFrom":makeQuery(id+"F1.opExtrude","CAP_EDGE",EDGE,{"disambiguationData":[OSD([subQ2]),TDD([subQ3])],"isStart":true})});}
            var Q17;
            Q17=makeQuery(id+"F1.opExtrude","CAP_EDGE",EDGE,{"disambiguationData":[OSD([sQuery(id+"F0.wireOp",EDGE,"E3")])],"isStart":true});
            var Q18;
            {var subQ0=sQuery(id+"F2.wireOp",EDGE,"E13");Q18=makeQuery(id+"F15.boolean.opBoolean","MERGE",EDGE,{"derivedFrom":[makeQuery(id+"F5.boolean.opBoolean","SPLIT",EDGE,{"disambiguationData":[TD([makeQuery(id+"F3.boolean.opBoolean","COPY",FACE,{"derivedFrom":makeQuery(id+"F3.opExtrude","SWEPT_FACE",FACE,{"disambiguationData":[OSD([sQuery(id+"F2.wireOp",EDGE,"E12")])]})})])],"derivedFrom":makeQuery(id+"F3.boolean.opBoolean","COPY",EDGE,{"derivedFrom":makeQuery(id+"F3.opExtrude","CAP_EDGE",EDGE,{"disambiguationData":[OSD([subQ0])],"isStart":true})})}),makeQuery(id+"F15.opExtrude","CAP_EDGE",EDGE,{"disambiguationData":[OSD([sQuery(id+"F14.wireOp",EDGE,"E53")])],"isStart":true})]});}
            var Q19;
            Q19=makeQuery(id+"F5.boolean.opBoolean","COPY",EDGE,{"derivedFrom":makeQuery(id+"F5.opExtrude","SWEPT_EDGE",EDGE,{"disambiguationData":[OSD([sQuery(id+"F0.wireOp",EDGE,"E2"),sQuery(id+"F4.wireOp",EDGE,"E20"),sQuery(id+"F4.wireOp",EDGE,"E21")])]})});
            var Q20;
            Q20=makeQuery(id+"F5.boolean.opBoolean","COPY",EDGE,{"derivedFrom":makeQuery(id+"F5.opExtrude","SWEPT_EDGE",EDGE,{"disambiguationData":[OSD([sQuery(id+"F0.wireOp",EDGE,"E2"),sQuery(id+"F4.wireOp",EDGE,"E19"),sQuery(id+"F4.wireOp",EDGE,"E20")])]})});
            fillet(context, id + "F27", {"entities" : qUnion([Q0, Q1, Q2, Q3, Q4, Q5, Q6, Q7, Q8, Q9, Q10, Q11, Q12, Q13, Q14, Q15, Q16, Q17, Q18, Q19, Q20]), "radius" : 2 * mm, "tangentPropagation" : true, "allowEdgeOverflow" : false});
        }
        {
            var Q0;
            Q0=makeQuery(id+"F15.boolean.opBoolean","MERGE",EDGE,{"derivedFrom":[makeQuery(id+"F3.boolean.opBoolean","COPY",EDGE,{"derivedFrom":makeQuery(id+"F3.opExtrude","CAP_EDGE",EDGE,{"disambiguationData":[OSD([sQuery(id+"F2.wireOp",EDGE,"E13")])],"isStart":false})}),makeQuery(id+"F15.opExtrude","CAP_EDGE",EDGE,{"disambiguationData":[OSD([sQuery(id+"F14.wireOp",EDGE,"E49")])],"isStart":false}),makeQuery(id+"F15.opExtrude","CAP_EDGE",EDGE,{"disambiguationData":[OSD([sQuery(id+"F14.wireOp",EDGE,"E53")])],"isStart":false})]});
            chamfer(context, id + "F28", {"entities" : qUnion([Q0]), "width" : 12 * mm, "tangentPropagation" : true});
        }
        {
            var Q0;
            {var subQ0=sQuery(id+"F14.wireOp",EDGE,"E53");var subQ1=sQuery(id+"F2.wireOp",EDGE,"E13");Q0=makeQuery(id+"F19.boolean.opBoolean","MERGE",FACE,{"derivedFrom":[makeQuery(id+"F17.boolean.opBoolean","MERGE",FACE,{"derivedFrom":[makeQuery(id+"F15.boolean.opBoolean","MERGE",FACE,{"derivedFrom":[makeQuery(id+"F3.boolean.opBoolean","COPY",FACE,{"derivedFrom":makeQuery(id+"F3.opExtrude","CAP_FACE",FACE,{"disambiguationData":[OSD([sQuery(id+"F0.wireOp",EDGE,"E6"),sQuery(id+"F0.wireOp",EDGE,"E7"),sQuery(id+"F0.wireOp",EDGE,"E8"),sQuery(id+"F0.wireOp",EDGE,"E9"),sQuery(id+"F2.wireOp",EDGE,"E12"),subQ1,sQuery(id+"F2.wireOp",EDGE,"E14"),sQuery(id+"F2.wireOp",EDGE,"E15"),sQuery(id+"F2.wireOp",EDGE,"E16"),sQuery(id+"F2.wireOp",EDGE,"E17")])],"isStart":false})}),makeQuery(id+"F15.opExtrude","CAP_FACE",FACE,{"disambiguationData":[OSD([sQuery(id+"F14.wireOp",EDGE,"E48"),sQuery(id+"F14.wireOp",EDGE,"E49"),sQuery(id+"F14.wireOp",EDGE,"E50")])],"isStart":false}),makeQuery(id+"F15.opExtrude","CAP_FACE",FACE,{"disambiguationData":[OSD([sQuery(id+"F14.wireOp",EDGE,"E51"),sQuery(id+"F14.wireOp",EDGE,"E52"),subQ0])],"isStart":false})]}),makeQuery(id+"F17.opExtrude","CAP_FACE",FACE,{"disambiguationData":[OSD([sQuery(id+"F0.wireOp",EDGE,"E10"),sQuery(id+"F16.wireOp",EDGE,"E54"),sQuery(id+"F16.wireOp",EDGE,"E57"),sQuery(id+"F16.wireOp",EDGE,"E58")])],"isStart":false})]}),makeQuery(id+"F19.opExtrude","CAP_FACE",FACE,{"disambiguationData":[OSD([sQuery(id+"F0.wireOp",EDGE,"E0.right"),sQuery(id+"F0.wireOp",EDGE,"E11"),subQ1,subQ0,sQuery(id+"F18.wireOp",EDGE,"E59")])],"isStart":false})]});}
            var sketch = newSketch(context, id + "F29", { "sketchPlane" : qUnion([Q0])});
            skLineSegment(sketch, "E68.bottom", {"start": v(-36.85, -0.58) * mm, "end": v(21.4, -0.58) * mm});
            skLineSegment(sketch, "E68.top", {"start": v(-36.85, 11.42) * mm, "end": v(21.4, 11.42) * mm});
            skLineSegment(sketch, "E68.left", {"start": v(-36.85, -0.58) * mm, "end": v(-36.85, 11.42) * mm});
            skLineSegment(sketch, "E68.right", {"start": v(21.4, -0.58) * mm, "end": v(21.4, 11.42) * mm});
            skSolve(sketch);
        }
        {
            var Q0;
            Q0 = qSketchRegion(id + "F29", true);
            extrude(context, id + "F30", {"entities" : qUnion([Q0]), "operationType" : NewBodyOperationType.REMOVE, "depth" : 25 * mm, "offsetDistance" : 25 * mm});
        }
        {
            var Q0;
            Q0=makeQuery(id+"F30.boolean.opBoolean","INTERSECT",EDGE,{"derivedFrom":[makeQuery(id+"F28.opChamfer","BLEND_FACE",FACE,{"disambiguationData":[OSD([sQuery(id+"F2.wireOp",EDGE,"E13"),sQuery(id+"F14.wireOp",EDGE,"E49"),sQuery(id+"F14.wireOp",EDGE,"E53")])]}),makeQuery(id+"F30.opExtrude","SWEPT_FACE",FACE,{"disambiguationData":[OSD([sQuery(id+"F29.wireOp",EDGE,"E68.left")])]})]});
            var Q1;
            Q1=makeQuery(id+"F30.boolean.opBoolean","INTERSECT",EDGE,{"derivedFrom":[makeQuery(id+"F28.opChamfer","BLEND_FACE",FACE,{"disambiguationData":[OSD([sQuery(id+"F2.wireOp",EDGE,"E13"),sQuery(id+"F14.wireOp",EDGE,"E49"),sQuery(id+"F14.wireOp",EDGE,"E53")])]}),makeQuery(id+"F30.opExtrude","SWEPT_FACE",FACE,{"disambiguationData":[OSD([sQuery(id+"F29.wireOp",EDGE,"E68.right")])]})]});
            var Q2;
            Q2=makeQuery(id+"F30.boolean.opBoolean","COPY",EDGE,{"derivedFrom":makeQuery(id+"F30.opExtrude","CAP_EDGE",EDGE,{"disambiguationData":[OSD([sQuery(id+"F29.wireOp",EDGE,"E68.top")])],"isStart":true})});
            fillet(context, id + "F31", {"entities" : qUnion([Q0, Q1, Q2]), "radius" : 2 * mm, "tangentPropagation" : true, "allowEdgeOverflow" : false});
        }
    });
